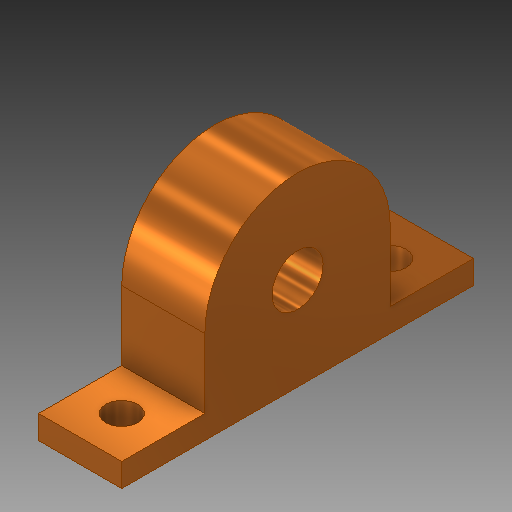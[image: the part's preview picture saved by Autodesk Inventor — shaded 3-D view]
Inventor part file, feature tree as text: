
AUTODESK INVENTOR PART (.ipt)
format: ipt  version: 2019 (Build 230136000, 136)  size: 140,800 bytes
history: native  units: in
note: dims shown in document units (in); Inventor stores cm internally (conversion verified against a paired STEP export)
features: extrude x2, sketch x2
ambient origin geometry x8: Origin, YZ Plane, XZ Plane, XY Plane, X Axis, Y Axis, Z Axis, Center Point
bodies: Solid1 (feature_tree)
feature tree (4):
  extrude  "Extrusion1"  Depth=2.1654in
  extrude  "Extrusion2"  Depth=0.5118in
  sketch  "Sketch1"  dims[d0=2.1654in d2=0.315in]
  sketch  "Sketch2"  dims[d3=0.5118in d4=0.0in d5=0.1969in d6=0.1969in d7=0.5118in d8=0.0in]
